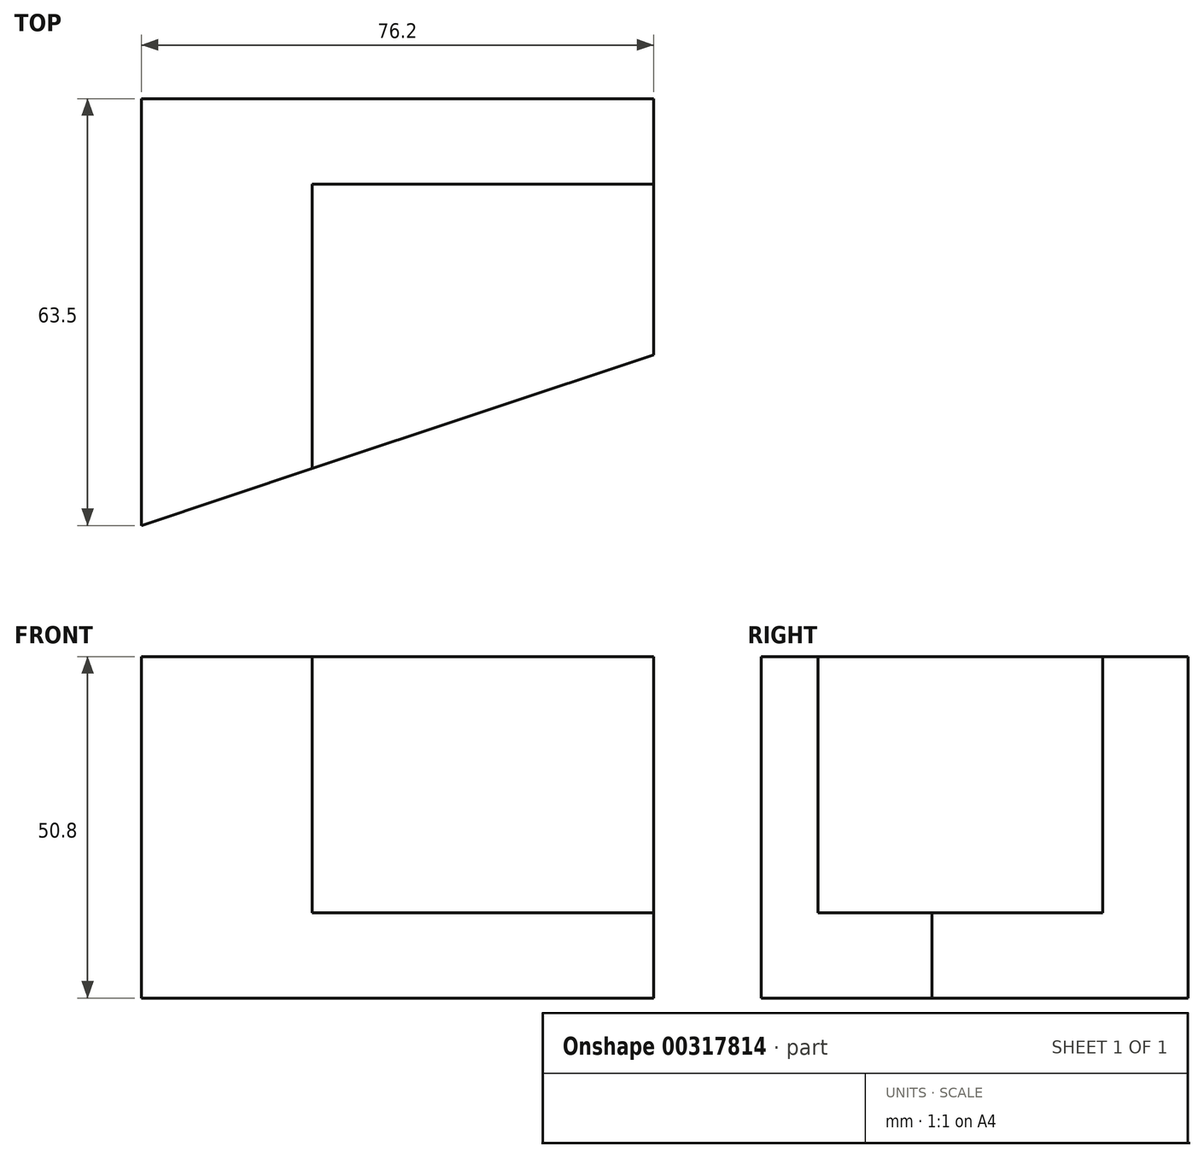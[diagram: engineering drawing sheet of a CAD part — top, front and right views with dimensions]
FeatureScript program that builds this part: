
annotation { "Feature Type Name" : "Feature", "Feature Type Description" : "" }
export const myFeature = defineFeature(function(context is Context, id is Id, definition is map)
    precondition{}
    {
        {
            var Q0;
            Q0=qCreatedBy(makeId("Top.planeOp"),FACE);
            var sketch = newSketch(context, id + "F0", { "sketchPlane" : qUnion([Q0])});
            skLineSegment(sketch, "E0", {"start": v(0, 0) * mm, "end": v(0, 63.5) * mm});
            skLineSegment(sketch, "E1", {"start": v(0, 63.5) * mm, "end": v(76.2, 63.5) * mm});
            skLineSegment(sketch, "E2", {"start": v(76.2, 63.5) * mm, "end": v(76.2, 25.4) * mm});
            skLineSegment(sketch, "E3", {"start": v(76.2, 25.4) * mm, "end": v(0, 0) * mm});
            skSolve(sketch);
        }
        {
            var Q0;
            Q0 = qSketchRegion(id + "F0", true);
            extrude(context, id + "F1", {"entities" : qUnion([Q0]), "depth" : 50.8 * mm});
        }
        {
            var Q0;
            Q0=qCreatedBy(makeId("Front.planeOp"),FACE);
            var sketch = newSketch(context, id + "F2", { "sketchPlane" : qUnion([Q0])});
            skLineSegment(sketch, "E4.bottom", {"start": v(76.2, 12.7) * mm, "end": v(25.4, 12.7) * mm});
            skLineSegment(sketch, "E4.top", {"start": v(76.2, 50.8) * mm, "end": v(25.4, 50.8) * mm});
            skLineSegment(sketch, "E4.left", {"start": v(76.2, 12.7) * mm, "end": v(76.2, 50.8) * mm});
            skLineSegment(sketch, "E4.right", {"start": v(25.4, 12.7) * mm, "end": v(25.4, 50.8) * mm});
            skSolve(sketch);
        }
        {
            var Q0;
            Q0 = qSketchRegion(id + "F2", true);
            extrude(context, id + "F3", {"entities" : qUnion([Q0]), "operationType" : NewBodyOperationType.REMOVE, "oppositeDirection" : true, "depth" : 50.8 * mm});
        }
    });
